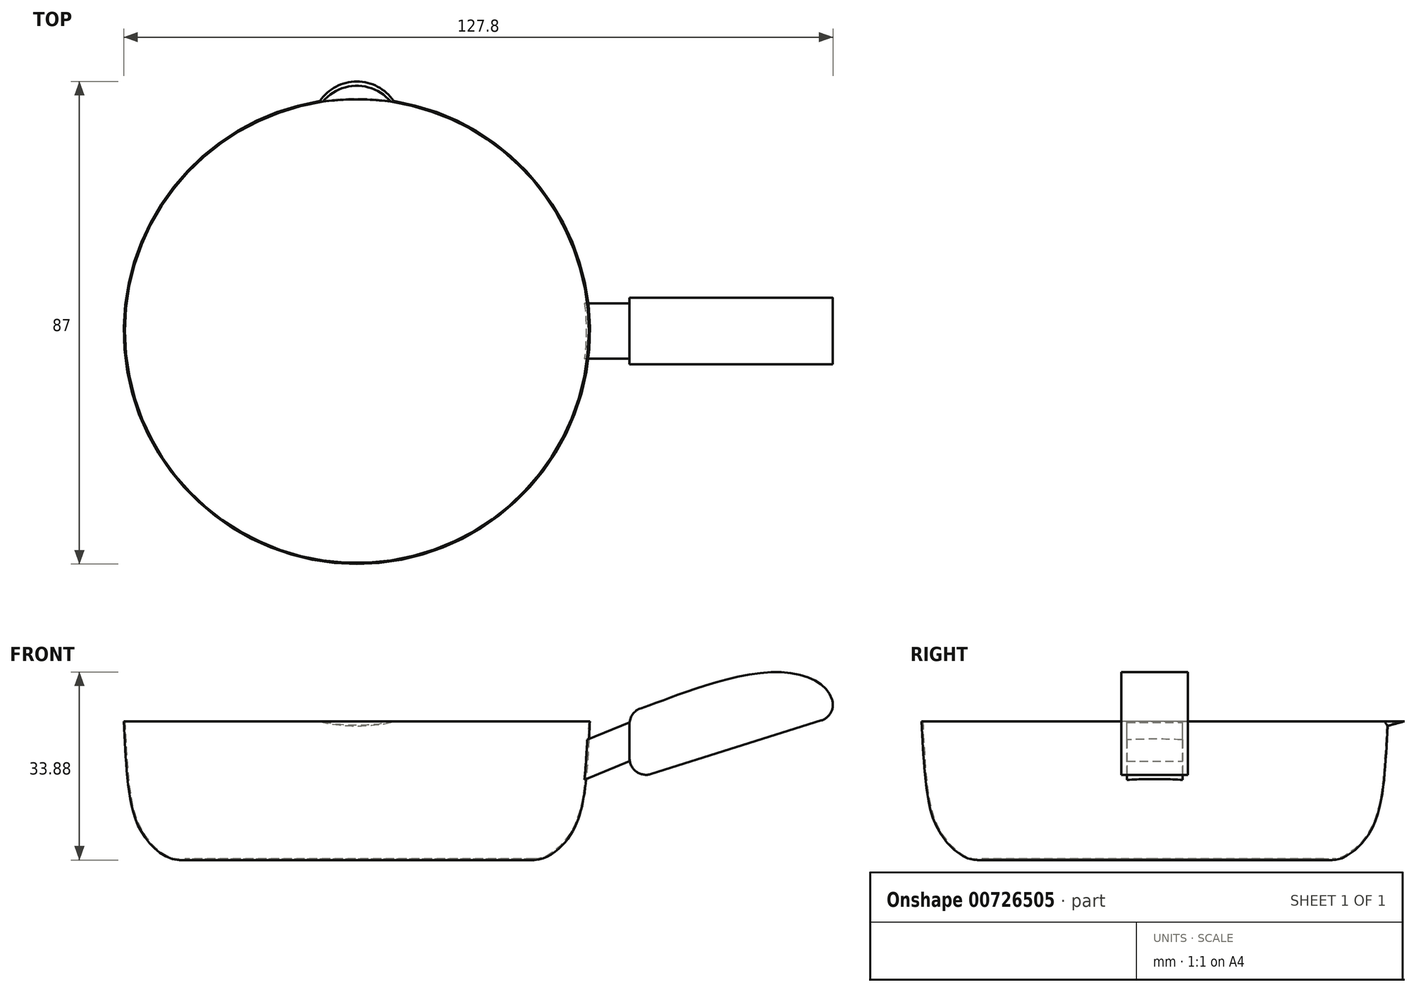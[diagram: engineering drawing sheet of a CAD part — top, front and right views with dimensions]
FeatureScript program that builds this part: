
annotation { "Feature Type Name" : "Feature", "Feature Type Description" : "" }
export const myFeature = defineFeature(function(context is Context, id is Id, definition is map)
    precondition{}
    {
        {
            var Q0;
            Q0=qCreatedBy(makeId("Front.planeOp"),FACE);
            var sketch = newSketch(context, id + "F0", { "sketchPlane" : qUnion([Q0])});
            skLineSegment(sketch, "E0", {"start": v(32, 0) * mm, "end": v(0, 0) * mm});
            skLineSegment(sketch, "E1", {"start": v(0, 0) * mm, "end": v(0, 25) * mm});
            skLineSegment(sketch, "E2", {"start": v(0, 25) * mm, "end": v(42, 25) * mm});
            skFitSpline(sketch, "E3", {"points": [v(42, 25) * mm, v(38.42, 4.42) * mm, v(32, 0) * mm], "startDerivative": vector(-2.68, -56.13) * mm, "endDerivative": vector(-18.85, 0) * mm});
            skSolve(sketch);
        }
        {
            var Q0;
            Q0 = qSketchRegion(id + "F0", true);
            var Q1;
            Q1=sQuery(id+"F0.wireOp",EDGE,"E1");
            revolve(context, id + "F1", {"surfaceOperationType" : NewSurfaceOperationType.NEW, "entities" : qUnion([Q0]), "axis" : qUnion([Q1]), "revolveType" : RevolveType.FULL});
        }
        {
            var Q0;
            Q0=qCreatedBy(makeId("Front.planeOp"),FACE);
            var sketch = newSketch(context, id + "F2", { "sketchPlane" : qUnion([Q0])});
            skLineSegment(sketch, "E4", {"start": v(39.9, 21) * mm, "end": v(39.9, 14) * mm});
            skLineSegment(sketch, "E5", {"start": v(39.9, 14) * mm, "end": v(49.14, 17.8) * mm});
            skLineSegment(sketch, "E6", {"start": v(49.14, 17.8) * mm, "end": v(49.14, 24.8) * mm});
            skLineSegment(sketch, "E7", {"start": v(39.9, 21) * mm, "end": v(49.14, 24.8) * mm});
            skLineSegment(sketch, "E8", {"start": v(39.9, 25) * mm, "end": v(39.9, 0) * mm, "construction": true});
            skSolve(sketch);
        }
        {
            var Q0;
            Q0 = qSketchRegion(id + "F2", true);
            extrude(context, id + "F3", {"entities" : qUnion([Q0]), "endBound" : BoundingType.SYMMETRIC, "depth" : 10 * mm, "offsetDistance" : 25 * mm});
        }
        {
            var Q0;
            Q0=qCreatedBy(makeId("Front.planeOp"),FACE);
            var sketch = newSketch(context, id + "F4", { "sketchPlane" : qUnion([Q0])});
            skLineSegment(sketch, "E9", {"start": v(49.14, 26.72) * mm, "end": v(49.14, 14.27) * mm});
            skLineSegment(sketch, "E10", {"start": v(49.14, 14.27) * mm, "end": v(85.86, 25.84) * mm});
            skFitSpline(sketch, "E11", {"points": [v(49.14, 26.72) * mm, v(58.96, 30.19) * mm, v(76.06, 33.87) * mm, v(84.88, 30.46) * mm, v(85.86, 25.84) * mm], "startDerivative": vector(48.67, 14.65) * mm, "endDerivative": vector(-3.72, -25.76) * mm});
            skSolve(sketch);
        }
        {
            var Q0;
            Q0 = qSketchRegion(id + "F4", true);
            extrude(context, id + "F5", {"entities" : qUnion([Q0]), "endBound" : BoundingType.SYMMETRIC, "depth" : 12 * mm, "offsetDistance" : 25 * mm});
        }
        {
            var Q0;
            Q0=makeQuery(id+"F5.opExtrude","SWEPT_EDGE",EDGE,{"disambiguationData":[OSD([sQuery(id+"F4.wireOp",EDGE,"E10"),sQuery(id+"F4.wireOp",EDGE,"E11")])]});
            var Q1;
            Q1=makeQuery(id+"F5.opExtrude","SWEPT_EDGE",EDGE,{"disambiguationData":[OSD([sQuery(id+"F4.wireOp",EDGE,"E9"),sQuery(id+"F4.wireOp",EDGE,"E11")])]});
            var Q2;
            Q2=makeQuery(id+"F5.opExtrude","SWEPT_EDGE",EDGE,{"disambiguationData":[OSD([sQuery(id+"F4.wireOp",EDGE,"E9"),sQuery(id+"F4.wireOp",EDGE,"E10")])]});
            fillet(context, id + "F6", {"entities" : qUnion([Q0, Q1, Q2]), "radius" : 3 * mm, "tangentPropagation" : true, "allowEdgeOverflow" : false});
        }
        {
            var Q0;
            Q0=makeQuery(id+"F1.opRevolve","SWEPT_BODY",BODY,{"disambiguationData":[OSD([sQuery(id+"F0.wireOp",EDGE,"E0"),sQuery(id+"F0.wireOp",EDGE,"E1"),sQuery(id+"F0.wireOp",EDGE,"E2"),sQuery(id+"F0.wireOp",EDGE,"E3")])]});
            var Q1;
            Q1=makeQuery(id+"F3.opExtrude","SWEPT_BODY",BODY,{"disambiguationData":[OSD([sQuery(id+"F2.wireOp",EDGE,"E4"),sQuery(id+"F2.wireOp",EDGE,"E5"),sQuery(id+"F2.wireOp",EDGE,"E6"),sQuery(id+"F2.wireOp",EDGE,"E7")])]});
            booleanBodies(context, id + "F7", {"operationType" : BooleanOperationType.SUBTRACTION, "tools" : qUnion([Q0]), "targets" : qUnion([Q1]), "keepTools" : true});
        }
        {
            var Q0;
            Q0=makeQuery(id+"F3.opExtrude","SWEPT_BODY",BODY,{"disambiguationData":[OSD([sQuery(id+"F2.wireOp",EDGE,"E4"),sQuery(id+"F2.wireOp",EDGE,"E5"),sQuery(id+"F2.wireOp",EDGE,"E6"),sQuery(id+"F2.wireOp",EDGE,"E7")])]});
            var Q1;
            Q1=makeQuery(id+"F5.opExtrude","SWEPT_BODY",BODY,{"disambiguationData":[OSD([sQuery(id+"F4.wireOp",EDGE,"E9"),sQuery(id+"F4.wireOp",EDGE,"E10"),sQuery(id+"F4.wireOp",EDGE,"E11")])]});
            booleanBodies(context, id + "F8", {"operationType" : BooleanOperationType.SUBTRACTION, "tools" : qUnion([Q0]), "targets" : qUnion([Q1]), "keepTools" : true});
        }
        {
            var Q0;
            Q0=makeQuery(id+"F1.opRevolve","SWEPT_FACE",FACE,{"disambiguationData":[OSD([sQuery(id+"F0.wireOp",EDGE,"E2")])]});
            var sketch = newSketch(context, id + "F9", { "sketchPlane" : qUnion([Q0])});
            skArc(sketch, "E12", {"start": v(0, 45) * mm, "mid": v(5.66, 42.66) * mm, "end": v(8, 37) * mm});
            skLineSegment(sketch, "E13", {"start": v(0, 0) * mm, "end": v(8, 0) * mm});
            skLineSegment(sketch, "E14", {"start": v(8, 0) * mm, "end": v(8, 37) * mm});
            skArc(sketch, "E15.MirrorCS", {"start": v(0, 45) * mm, "mid": v(-5.66, 42.66) * mm, "end": v(-8, 37) * mm});
            skLineSegment(sketch, "E16.MirrorCS", {"start": v(-8, 0) * mm, "end": v(-8, 37) * mm});
            skLineSegment(sketch, "E17.MirrorCS", {"start": v(0, 0) * mm, "end": v(-8, 0) * mm});
            skSolve(sketch);
        }
        {
            var Q0;
            Q0=qCreatedBy(makeId("Right.planeOp"),FACE);
            var sketch = newSketch(context, id + "F10", { "sketchPlane" : qUnion([Q0])});
            skLineSegment(sketch, "E18", {"start": v(0, 25) * mm, "end": v(-7.73, 22.93) * mm});
            skSolve(sketch);
        }
        {
            var Q0;
            Q0 = qSketchRegion(id + "F9", true);
            var Q1;
            Q1 = qConstructionFilter(qBodyType(qCreatedBy(id + "F10" ,EDGE), BodyType.WIRE), ConstructionObject.NO);
            sweep(context, id + "F11", {"operationType" : NewBodyOperationType.ADD, "profiles" : qUnion([Q0]), "path" : qUnion([Q1])});
        }
        {
            var Q0;
            Q0=makeQuery(id+"F11.boolean.opBoolean","MERGE",FACE,{"derivedFrom":[makeQuery(id+"F1.opRevolve","SWEPT_FACE",FACE,{"disambiguationData":[OSD([sQuery(id+"F0.wireOp",EDGE,"E2")])]}),makeQuery(id+"F11.opSweep","CAP_FACE",FACE,{"disambiguationData":[OSD([sQuery(id+"F9.wireOp",EDGE,"E12"),sQuery(id+"F9.wireOp",EDGE,"E13"),sQuery(id+"F9.wireOp",EDGE,"E14"),sQuery(id+"F9.wireOp",EDGE,"E15.MirrorCS"),sQuery(id+"F9.wireOp",EDGE,"E16.MirrorCS"),sQuery(id+"F9.wireOp",EDGE,"E17.MirrorCS"),sQuery(id+"F10.wireOp",VERTEX,"E18.start")])],"isStart":true})]});
            shell(context, id + "F12", {"entities" : qUnion([Q0]), "thickness" : 0.2 * mm});
        }
    });
